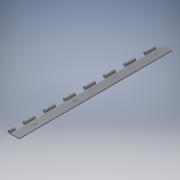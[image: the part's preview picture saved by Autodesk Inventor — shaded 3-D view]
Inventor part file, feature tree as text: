
AUTODESK INVENTOR PART (.ipt)
format: ipt  version: 2016 (Build 200138000, 138)  size: 183,808 bytes
history: native  units: mm
features: sketch x3, extrude x2, pattern_linear x1, hole x1
ambient origin geometry x8: Origin, YZ Plane, XZ Plane, XY Plane, X Axis, Y Axis, Z Axis, Center Point
bodies: Solid1 (feature_tree)
feature tree (7):
  extrude  "Extrusion1"  Depth=3.0mm
  extrude  "Extrusion2"  Depth=10.0mm
  pattern_linear  "Rectangular Pattern1"  Count1=2  [1 undecoded]
  hole  "Hole1"  [1 undecoded]
  sketch  "Sketch2"  dims[d0=1.5mm d1=1.5mm d2=20.0mm d3=3.0mm d4=4.712389mm]
  sketch  "Sketch3"  dims[d5=304.8mm d6=0.0mm d7=10.0mm d8=20.0mm]
  sketch  "Sketch4"  dims[d9=6.0mm d10=1800.0mm d11=0.0mm d12=250.0mm d14=40.0mm d15=8.0mm d16=3.0mm d17=6.0mm d18=6.0mm d19=2.0mm d20=90.0deg d21=8.0mm d22=20.594885mm]
note: 2 required parameter values undecoded (feature->parameter linkage not recoverable at this tier; creation-order binding heuristic only, values carry confidence <= 0.55)
